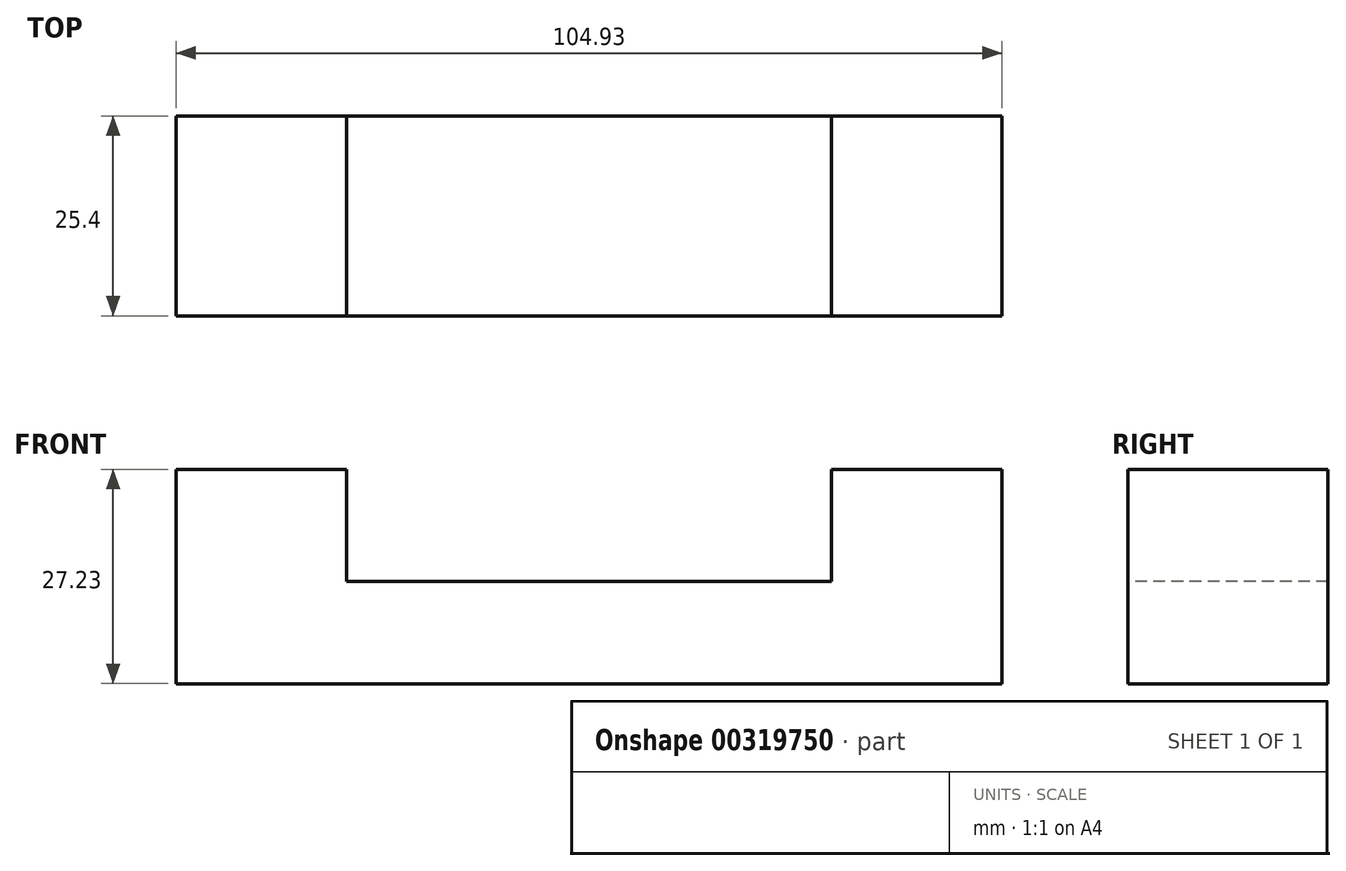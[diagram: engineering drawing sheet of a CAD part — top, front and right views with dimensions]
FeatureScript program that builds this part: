
annotation { "Feature Type Name" : "Feature", "Feature Type Description" : "" }
export const myFeature = defineFeature(function(context is Context, id is Id, definition is map)
    precondition{}
    {
        {
            var Q0;
            Q0=qCreatedBy(makeId("Front.planeOp"),FACE);
            var sketch = newSketch(context, id + "F0", { "sketchPlane" : qUnion([Q0])});
            skLineSegment(sketch, "E0", {"start": v(-58.8, 2.63) * mm, "end": v(-58.8, 20.58) * mm});
            skLineSegment(sketch, "E1", {"start": v(-58.8, 20.58) * mm, "end": v(-37.14, 20.58) * mm});
            skLineSegment(sketch, "E2", {"start": v(-37.14, 20.58) * mm, "end": v(-37.14, 6.35) * mm});
            skLineSegment(sketch, "E3", {"start": v(-37.14, 6.35) * mm, "end": v(24.45, 6.35) * mm});
            skLineSegment(sketch, "E4", {"start": v(24.45, 6.35) * mm, "end": v(24.45, 20.58) * mm});
            skLineSegment(sketch, "E5", {"start": v(24.45, 20.58) * mm, "end": v(46.12, 20.58) * mm});
            skLineSegment(sketch, "E6", {"start": v(46.12, 20.58) * mm, "end": v(46.12, 6.35) * mm});
            skLineSegment(sketch, "E7", {"start": v(46.12, 6.35) * mm, "end": v(46.12, -6.65) * mm});
            skLineSegment(sketch, "E8", {"start": v(46.12, -6.65) * mm, "end": v(-58.8, -6.65) * mm});
            skLineSegment(sketch, "E9", {"start": v(-58.8, -6.65) * mm, "end": v(-58.8, 2.63) * mm});
            skSolve(sketch);
        }
        {
            var Q0;
            Q0=makeQuery(id+"F0.imprint","IMPRINT",FACE,{"disambiguationData":[TD([[makeQuery(id+"F0.imprint","IMPRINT",EDGE,{"derivedFrom":sQuery(id+"F0.wireOp",EDGE,"E0")}),-1.0]])]});
            extrude(context, id + "F1", {"entities" : qUnion([Q0]), "oppositeDirection" : true, "depth" : 25.4 * mm});
        }
    });
